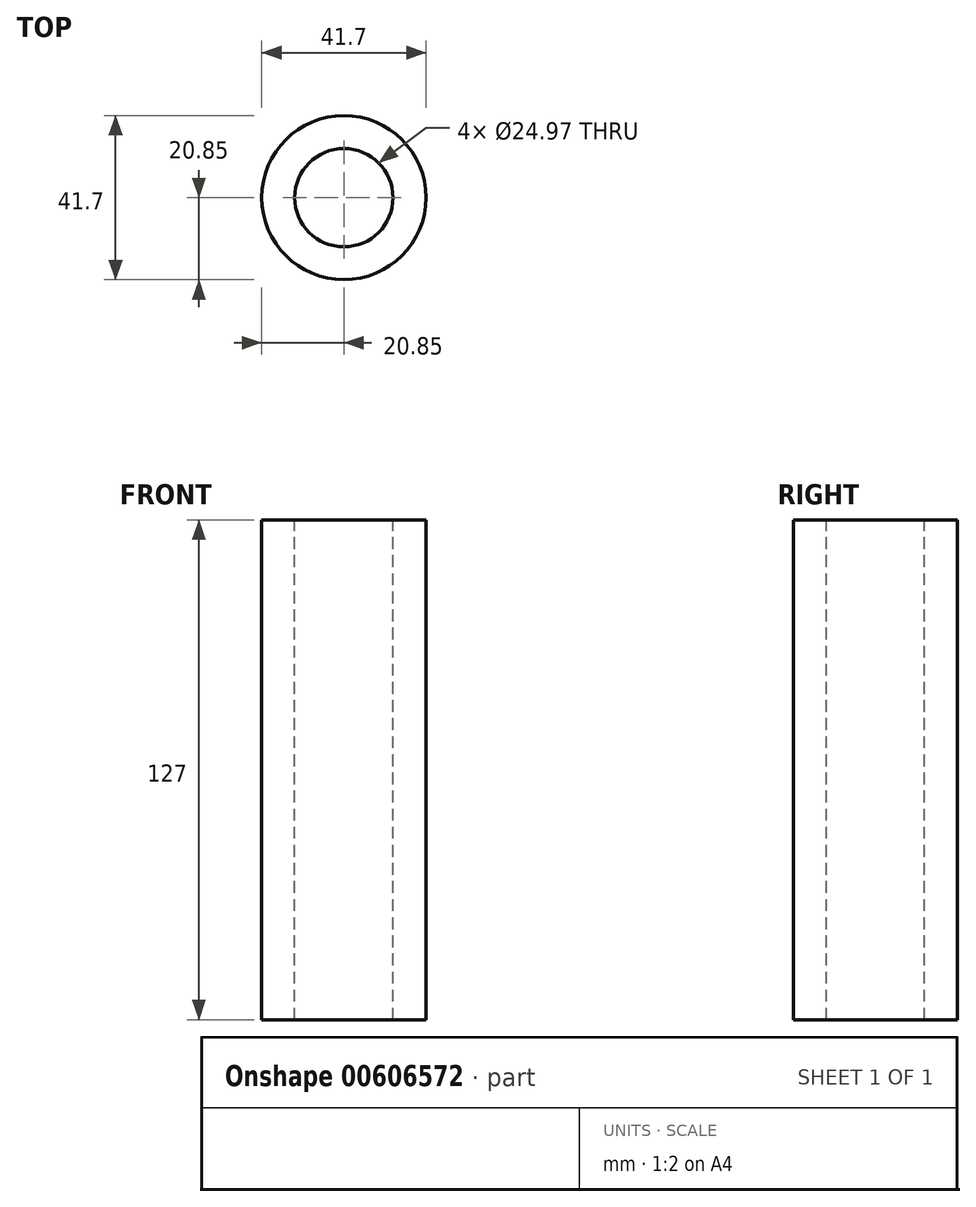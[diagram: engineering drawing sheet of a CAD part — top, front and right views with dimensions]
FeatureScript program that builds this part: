
annotation { "Feature Type Name" : "Feature", "Feature Type Description" : "" }
export const myFeature = defineFeature(function(context is Context, id is Id, definition is map)
    precondition{}
    {
        {
            var Q0;
            Q0=qCreatedBy(makeId("Top.planeOp"),FACE);
            var sketch = newSketch(context, id + "F0", { "sketchPlane" : qUnion([Q0])});
            skCircle(sketch, "E0", {"center": v(0, 0) * mm, "radius": 20.85 * mm});
            skSolve(sketch);
        }
        {
            var Q0;
            Q0=makeQuery(id+"F0.imprint","IMPRINT",FACE,{"disambiguationData":[TD([[makeQuery(id+"F0.imprint","IMPRINT",EDGE,{"derivedFrom":sQuery(id+"F0.wireOp",EDGE,"E0")}),1.0]])]});
            extrude(context, id + "F1", {"entities" : qUnion([Q0]), "depth" : 127 * mm, "offsetDistance" : 25.4 * mm});
        }
        {
            var Q0;
            Q0=qCreatedBy(makeId("Top.planeOp"),FACE);
            var sketch = newSketch(context, id + "F2", { "sketchPlane" : qUnion([Q0])});
            skCircle(sketch, "E1", {"center": v(0, 0) * mm, "radius": 9.38 * mm});
            skSolve(sketch);
        }
        {
            var Q0;
            Q0 = qSketchRegion(id + "F2", true);
            extrude(context, id + "F3", {"entities" : qUnion([Q0]), "operationType" : NewBodyOperationType.REMOVE, "oppositeDirection" : true, "depth" : 127 * mm, "offsetDistance" : 25.4 * mm});
        }
        {
            var Q0;
            Q0=makeQuery(id+"F1.opExtrude","CAP_FACE",FACE,{"disambiguationData":[OSD([sQuery(id+"F0.wireOp",EDGE,"E0")])],"isStart":false});
            var sketch = newSketch(context, id + "F4", { "sketchPlane" : qUnion([Q0])});
            skCircle(sketch, "E2", {"center": v(0, 0) * mm, "radius": 12.49 * mm});
            skSolve(sketch);
        }
        {
            var Q0;
            Q0 = qSketchRegion(id + "F4", true);
            extrude(context, id + "F5", {"entities" : qUnion([Q0]), "operationType" : NewBodyOperationType.REMOVE, "oppositeDirection" : true, "depth" : 127 * mm, "offsetDistance" : 25.4 * mm});
        }
    });
